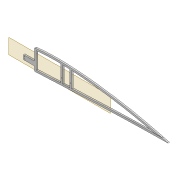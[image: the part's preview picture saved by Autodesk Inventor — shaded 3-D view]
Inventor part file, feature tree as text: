
AUTODESK INVENTOR PART (.ipt)
format: ipt  version: 2022 (Build 260153000, 153)  size: 429,056 bytes
history: native  units: mm
features: extrude x8, sketch x7, projected_geometry x6, fillet x2, shell x1, plane x1
ambient origin geometry x8: Origin, YZ Plane, XZ Plane, XY Plane, X Axis, Y Axis, Z Axis, Center Point
bodies: Solid1 (feature_tree)
feature tree (25):
  extrude  "Extrusion1"  Depth=5.0mm
  shell  "Shell1"  Thickness=2.0mm
  extrude  "Extrusion8"  Depth=5.9mm
  extrude  "Extrusion3"  Depth=10.0mm TaperAngle=0.0deg
  extrude  "Extrusion4"  Depth=2.0mm
  fillet  "Fillet1"  Radius=80.0mm
  sketch  "Sketch10"  dims[d22=4.0mm d23=0.0mm d31=2.0mm d62=80.0mm]
  extrude  "Extrusion5"  Depth=4.0mm TaperAngle=0.0deg
  plane  "Work Plane2"
  extrude  "Extrusion10"  Depth=12.0mm
  fillet  "Fillet2"  Radius=5.0mm
  extrude  "Extrusion11"  Depth=0.5mm
  extrude  "Extrusion12"  Depth=0.5mm
  sketch  "Sketch3"  dims[d0=4.0mm d1=0.0mm d2=5.0mm d7=2.0mm]
  sketch  "Sketch8"  dims[d8=2.0mm d9=5.9mm]
  sketch  "Sketch9"  dims[d13=10.0mm d14=0.0mm d16=10.0mm d17=0.0mm]
  projected_geometry  "Projected Loop4"
  projected_geometry  "Projected Loop10"
  sketch  "Sketch24"  dims[d63=6.0mm d64=4.0mm d65=0.0mm]
  projected_geometry  "Projected Loop11"
  projected_geometry  "Projected Loop12"
  projected_geometry  "Projected Loop13"
  sketch  "Sketch28"  dims[d66=3.0mm d67=12.0mm d68=5.0mm]
  projected_geometry  "Projected Loop14"
  sketch  "Sketch29"  dims[d69=5.0mm d74=12.0mm d75=30.0mm d76=3.05mm d77=5.0mm d78=10.0mm d79=0.0mm d80=2.0mm d81=100.0mm d82=20.0mm d83=1.6mm d84=1.6mm d85=2.5mm d86=2.5mm d87=0.5mm d88=10.0mm d89=0.0mm d90=10.0mm d91=0.0mm]
